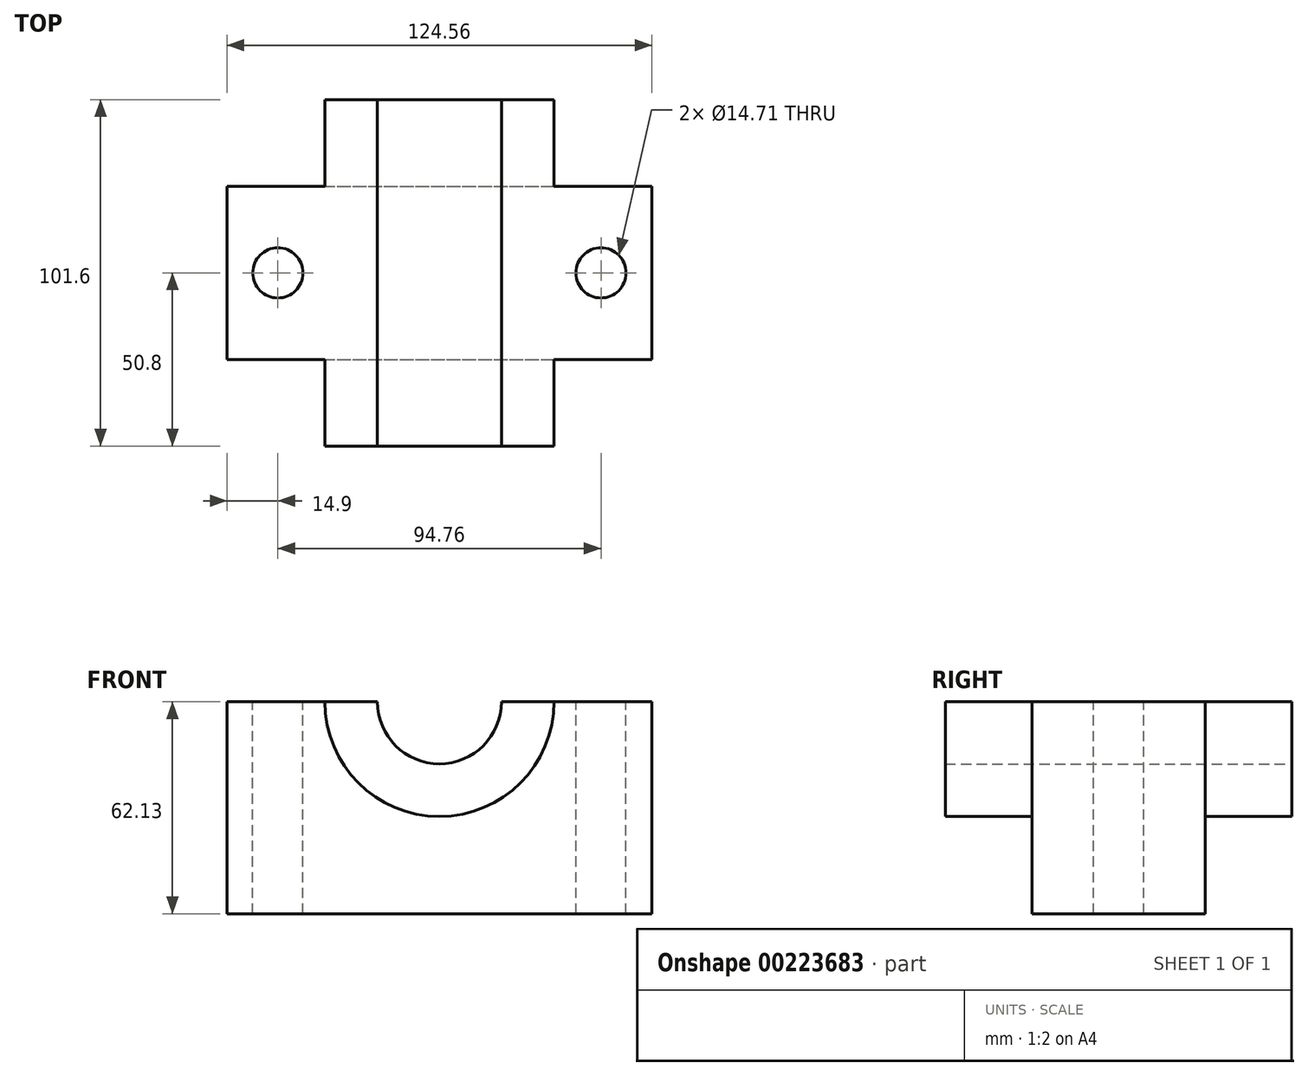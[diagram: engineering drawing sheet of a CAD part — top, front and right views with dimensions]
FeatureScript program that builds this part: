
annotation { "Feature Type Name" : "Feature", "Feature Type Description" : "" }
export const myFeature = defineFeature(function(context is Context, id is Id, definition is map)
    precondition{}
    {
        {
            var Q0;
            Q0=qCreatedBy(makeId("Front.planeOp"),FACE);
            var sketch = newSketch(context, id + "F0", { "sketchPlane" : qUnion([Q0])});
            skLineSegment(sketch, "E0.top", {"start": v(-62.28, -62.13) * mm, "end": v(62.28, -62.13) * mm});
            skLineSegment(sketch, "E0.left", {"start": v(-62.28, 0) * mm, "end": v(-62.28, -62.13) * mm});
            skLineSegment(sketch, "E0.right", {"start": v(62.28, 0) * mm, "end": v(62.28, -62.13) * mm});
            skPoint(sketch, "E0.middle", {"position": v(0, 0) * mm});
            skArc(sketch, "E1", {"start": v(-33.6, 0) * mm, "mid": v(0, -33.6) * mm, "end": v(33.6, 0) * mm});
            skArc(sketch, "E2", {"start": v(-18.18, 0) * mm, "mid": v(0, -18.18) * mm, "end": v(18.18, 0) * mm});
            skLineSegment(sketch, "E3", {"start": v(-62.28, 0) * mm, "end": v(-33.6, 0) * mm});
            skLineSegment(sketch, "E4.trimOffspring", {"start": v(18.18, 0) * mm, "end": v(62.28, 0) * mm});
            skPoint(sketch, "E0.bottom.end.orphan", {"position": v(62.28, 62.13) * mm});
            skPoint(sketch, "E5.orphan", {"position": v(-62.28, 62.13) * mm});
            skLineSegment(sketch, "E6", {"start": v(-18.18, 0) * mm, "end": v(-33.6, 0) * mm});
            skSolve(sketch);
        }
        {
            var Q0;
            Q0 = qSketchRegion(id + "F0", true);
            extrude(context, id + "F1", {"entities" : qUnion([Q0]), "depth" : 25.4 * mm});
        }
        {
            var Q0;
            {var subQ0=sQuery(id+"F0.wireOp",EDGE,"E1");Q0=makeQuery(id+"F0.imprint","IMPRINT",FACE,{"disambiguationData":[TD([[makeQuery(id+"F0.imprint","IMPRINT",EDGE,{"derivedFrom":subQ0}),1.0]])]});}
            extrude(context, id + "F2", {"entities" : qUnion([Q0]), "operationType" : NewBodyOperationType.ADD, "depth" : 50.8 * mm});
        }
        {
            var Q0;
            Q0=makeQuery(id+"F1.opExtrude","SWEPT_BODY",BODY,{"disambiguationData":[OSD([sQuery(id+"F0.wireOp",EDGE,"E0.top"),sQuery(id+"F0.wireOp",EDGE,"E0.left"),sQuery(id+"F0.wireOp",EDGE,"E0.right"),sQuery(id+"F0.wireOp",EDGE,"E2"),sQuery(id+"F0.wireOp",EDGE,"E3"),sQuery(id+"F0.wireOp",EDGE,"E4.trimOffspring"),sQuery(id+"F0.wireOp",EDGE,"E6")])]});
            var Q1;
            Q1=qCreatedBy(makeId("Front.planeOp"),FACE);
            mirror(context, id + "F3", {"operationType" : NewBodyOperationType.ADD, "entities" : qUnion([Q0]), "mirrorPlane" : qUnion([Q1])});
        }
        {
            var Q0;
            {var subQ0=sQuery(id+"F0.wireOp",EDGE,"E6");var subQ1=makeQuery(id+"F2.boolean.opBoolean","MERGE",FACE,{"derivedFrom":[makeQuery(id+"F1.opExtrude","SWEPT_FACE",FACE,{"disambiguationData":[OSD([sQuery(id+"F0.wireOp",EDGE,"E3"),subQ0])]}),makeQuery(id+"F2.opExtrude","SWEPT_FACE",FACE,{"disambiguationData":[OSD([subQ0])]})]});Q0=makeQuery(id+"F3.boolean.opBoolean","MERGE",FACE,{"derivedFrom":[subQ1,makeQuery(id+"F3.opPattern","COPY",FACE,{"derivedFrom":subQ1,"instanceName":"1"})]});}
            var sketch = newSketch(context, id + "F4", { "sketchPlane" : qUnion([Q0])});
            skLineSegment(sketch, "E7", {"start": v(0, 0) * mm, "end": v(0, 43.36) * mm});
            skCircle(sketch, "E8", {"center": v(-47.38, 0) * mm, "radius": 7.36 * mm});
            skPoint(sketch, "E8.centerSnap0", {"position": v(-62.28, 0) * mm});
            skCircle(sketch, "E9.MirrorC", {"center": v(47.38, 0) * mm, "radius": 7.36 * mm});
            skSolve(sketch);
        }
        {
            var Q0;
            Q0 = qSketchRegion(id + "F4", true);
            extrude(context, id + "F5", {"entities" : qUnion([Q0]), "operationType" : NewBodyOperationType.REMOVE, "endBound" : BoundingType.THROUGH_ALL, "oppositeDirection" : true, "depth" : 25.4 * mm});
        }
    });
